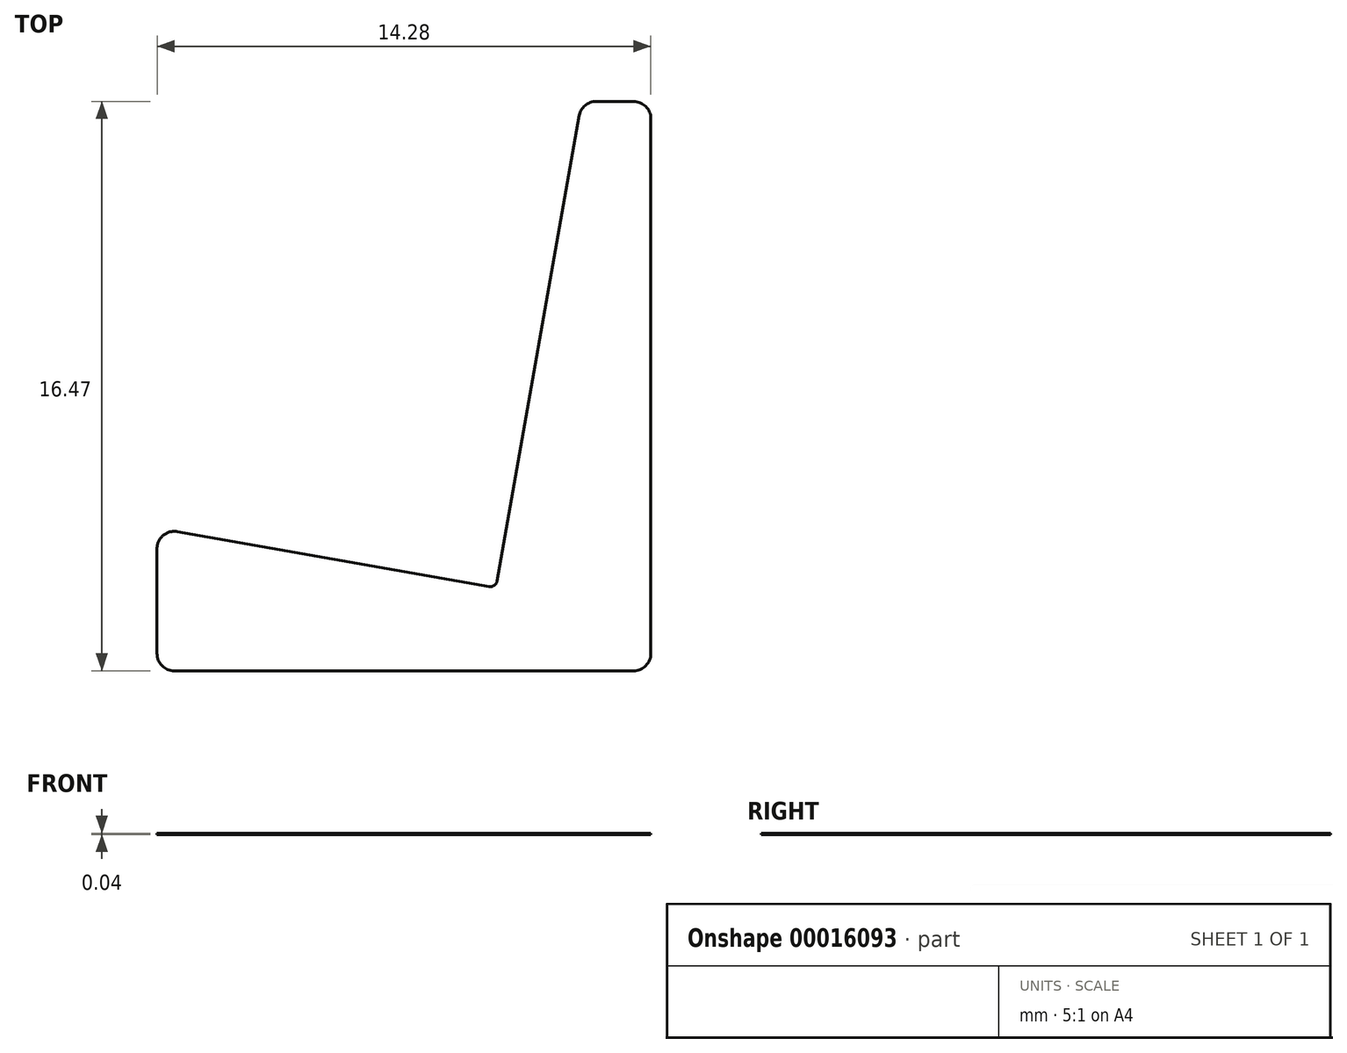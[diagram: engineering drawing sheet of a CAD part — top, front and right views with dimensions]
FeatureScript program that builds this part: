
annotation { "Feature Type Name" : "Feature", "Feature Type Description" : "" }
export const myFeature = defineFeature(function(context is Context, id is Id, definition is map)
    precondition{}
    {
        {
            var Q0;
            Q0=qCreatedBy(makeId("Top.planeOp"),FACE);
            var sketch = newSketch(context, id + "F0", { "sketchPlane" : qUnion([Q0])});
            skLineSegment(sketch, "E0", {"start": v(2.47, 2.43) * mm, "end": v(-6.56, 4.03) * mm});
            skLineSegment(sketch, "E1", {"start": v(-7.14, 3.53) * mm, "end": v(-7.14, 0) * mm});
            skLineSegment(sketch, "E2", {"start": v(-7.14, 0) * mm, "end": v(7.14, 0) * mm});
            skLineSegment(sketch, "E3", {"start": v(7.14, 0) * mm, "end": v(7.14, 15.97) * mm});
            skLineSegment(sketch, "E4", {"start": v(2.7, 2.6) * mm, "end": v(5.07, 16.06) * mm});
            skLineSegment(sketch, "E5", {"start": v(5.56, 16.47) * mm, "end": v(6.64, 16.47) * mm});
            skPoint(sketch, "E6.visualSharp", {"position": v(5.14, 16.47) * mm});
            skArc(sketch, "E6.filletArc", {"start": v(5.56, 16.47) * mm, "mid": v(5.24, 16.35) * mm, "end": v(5.07, 16.06) * mm});
            skPoint(sketch, "E7.visualSharp", {"position": v(7.14, 16.47) * mm});
            skArc(sketch, "E7.filletArc", {"start": v(7.14, 15.97) * mm, "mid": v(7, 16.32) * mm, "end": v(6.64, 16.47) * mm});
            skPoint(sketch, "E8.visualSharp", {"position": v(-7.14, 4.13) * mm});
            skArc(sketch, "E8.filletArc", {"start": v(-6.56, 4.03) * mm, "mid": v(-6.97, 3.92) * mm, "end": v(-7.14, 3.53) * mm});
            skPoint(sketch, "E9.visualSharp", {"position": v(2.66, 2.4) * mm});
            skArc(sketch, "E9.filletArc", {"start": v(2.47, 2.43) * mm, "mid": v(2.62, 2.47) * mm, "end": v(2.7, 2.6) * mm});
            skArc(sketch, "E10.0", {"start": v(2.33, 1.65) * mm, "mid": v(3.07, 1.81) * mm, "end": v(3.49, 2.46) * mm});
            skLineSegment(sketch, "E10.1", {"start": v(2.33, 1.65) * mm, "end": v(-6.34, 3.18) * mm});
            skLineSegment(sketch, "E10.3", {"start": v(-6.34, 3.18) * mm, "end": v(-6.34, 0.8) * mm});
            skLineSegment(sketch, "E10.4", {"start": v(-6.34, 0.8) * mm, "end": v(6.34, 0.8) * mm});
            skLineSegment(sketch, "E10.5", {"start": v(3.49, 2.46) * mm, "end": v(5.82, 15.67) * mm});
            skLineSegment(sketch, "E10.6", {"start": v(6.34, 0.8) * mm, "end": v(6.34, 15.67) * mm});
            skLineSegment(sketch, "E10.8", {"start": v(5.82, 15.67) * mm, "end": v(6.34, 15.67) * mm});
            skSolve(sketch);
        }
        {
            var Q0;
            Q0=qSketchRegion(id+"F0",true);
            var Q1;
            Q1=makeQuery(id+"F0.imprint","IMPRINT",FACE,{"disambiguationData":[TD([[makeQuery(id+"F0.imprint","IMPRINT",EDGE,{"derivedFrom":sQuery(id+"F0.wireOp",EDGE,"E10.0")}),-1.0]])]});
            extrude(context, id + "F1", {"entities" : qUnion([Q0, Q1]), "depth" : 17 / 406.4 * mm});
        }
        {
            var Q0;
            Q0=makeQuery(id+"F1.opExtrude","SWEPT_EDGE",EDGE,{"disambiguationData":[OSD([sQuery(id+"F0.wireOp",EDGE,"E4"),sQuery(id+"F0.wireOp",EDGE,"E5")])]});
            var Q1;
            Q1=makeQuery(id+"F1.opExtrude","SWEPT_EDGE",EDGE,{"disambiguationData":[OSD([sQuery(id+"F0.wireOp",EDGE,"E0"),sQuery(id+"F0.wireOp",EDGE,"E1")])]});
            var Q2;
            Q2=makeQuery(id+"F1.opExtrude","SWEPT_EDGE",EDGE,{"disambiguationData":[OSD([sQuery(id+"F0.wireOp",EDGE,"E3"),sQuery(id+"F0.wireOp",EDGE,"E5")])]});
            fillet(context, id + "F2", {"entities" : qUnion([Q0, Q1, Q2]), "radius" : .5 * mm, "tangentPropagation" : true, "allowEdgeOverflow" : false});
        }
    });
